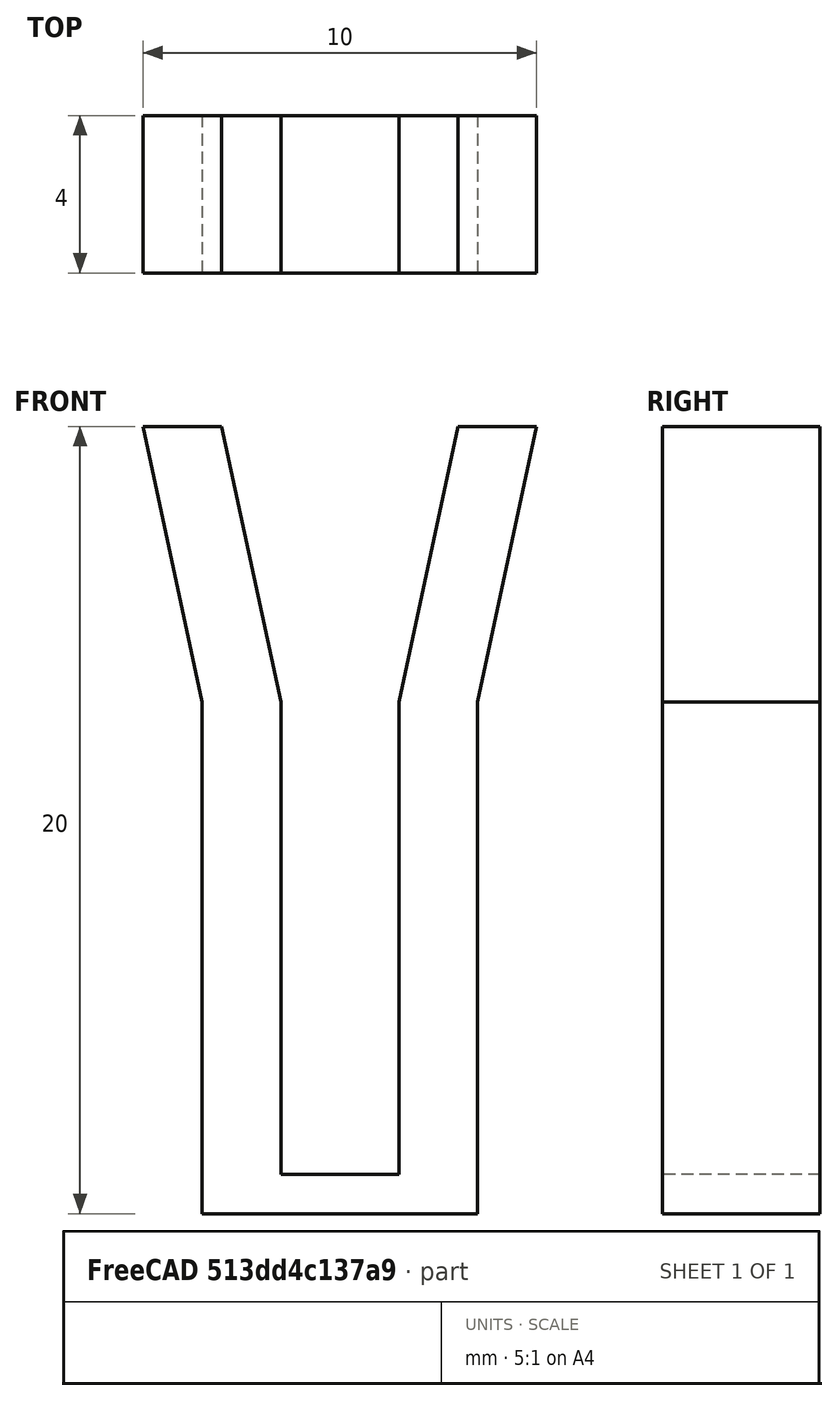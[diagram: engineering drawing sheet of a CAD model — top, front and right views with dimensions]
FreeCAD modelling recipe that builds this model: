
FCSTD DOCUMENT  (FreeCAD 0.15R4671 (Git))
Label: Guide Vee
License: All rights reserved
LicenseURL: http://en.wikipedia.org/wiki/All_rights_reserved
objects: Sketcher::SketchObject×1, PartDesign::Pad×1
note: 3 computed .brp shape members not serialized (recipe doc carries the construction recipe); baked Part::Feature solids carry a one-line shape summary decoded from their .brp

FEATURE [Sketcher::SketchObject] Sketch  label="Vee Support"
  Placement = pos=(0,0,0) rot=(1,0,0;1.5708rad)
  sketch-geometry (13):
    g0: LineSegment StartX=3 StartY=19 StartZ=0 EndX=1.5 EndY=12 EndZ=0
    g1: LineSegment StartX=1.5 StartY=12 StartZ=0 EndX=1.5 EndY=0 EndZ=0
    g2: LineSegment StartX=1.5 StartY=0 StartZ=0 EndX=-1.5 EndY=0 EndZ=0
    g3: LineSegment StartX=-1.5 StartY=0 StartZ=0 EndX=-1.5 EndY=12 EndZ=0
    g4: LineSegment StartX=-1.5 StartY=12 StartZ=0 EndX=-3 EndY=19 EndZ=0
    g5: LineSegment StartX=-3 StartY=19 StartZ=0 EndX=-5 EndY=19 EndZ=0
    g6: LineSegment StartX=-5 StartY=19 StartZ=0 EndX=-3.5 EndY=12 EndZ=0
    g7: LineSegment StartX=-3.5 StartY=12 StartZ=0 EndX=-3.5 EndY=-1 EndZ=0
    g8: LineSegment StartX=-3.5 StartY=-1 StartZ=0 EndX=3.5 EndY=-1 EndZ=0
    g9: LineSegment StartX=3.5 StartY=-1 StartZ=0 EndX=3.5 EndY=12 EndZ=0
    g10: LineSegment StartX=3.5 StartY=12 StartZ=0 EndX=5 EndY=19 EndZ=0
    g11: LineSegment StartX=5 StartY=19 StartZ=0 EndX=3 EndY=19 EndZ=0
    g12: LineSegment [constr] StartX=-3.5 StartY=12 StartZ=0 EndX=-1.5 EndY=12 EndZ=0
  constraints (35):
    c: Coincident(g0,g1)
    c: Coincident(g1,g2)
    c: Coincident(g2,g3)
    c: Coincident(g3,g4)
    c: Coincident(g4,g5)
    c: Coincident(g5,g6)
    c: Coincident(g6,g7)
    c: Coincident(g7,g8)
    c: Coincident(g8,g9)
    c: Coincident(g9,g10)
    c: Coincident(g10,g11)
    c: Coincident(g11,g0)
    c: Horizontal(g11)
    c: Horizontal(g5)
    c: Horizontal(g2)
    c: Horizontal(g8)
    c: Vertical(g3)
    c: Vertical(g1)
    c: Vertical(g9)
    c: Parallel(g6,g4)
    c: Parallel(g0,g10)
    c: Symmetric(g3,g0,g-2)
    c: Symmetric(g4,g0,g-2)
    c: DistanceX(g2) = -3
    c: DistanceX(g2,g7) = -2
    c: Symmetric(g7,g8,g-2)
    c: Symmetric(g6,g9,g-2)
    c: Horizontal(g12)
    c: Coincident(g6,g12)
    c: Coincident(g12,g3)
    c: DistanceY(g2,g7) = -1
    c: DistanceY(g5,g7) = -20
    c: DistanceY(g3,g2) = -12
    c: DistanceX(g4,g0) = 6
    c: PointOnObject(g2,g-1)
FEATURE [PartDesign::Pad] Pad
  Length = 4
  Length2 = 100
  Placement = pos=(0,0,0) rot=(1,0,0;1.5708rad)
  Sketch = -> Sketch
  Type = 0
